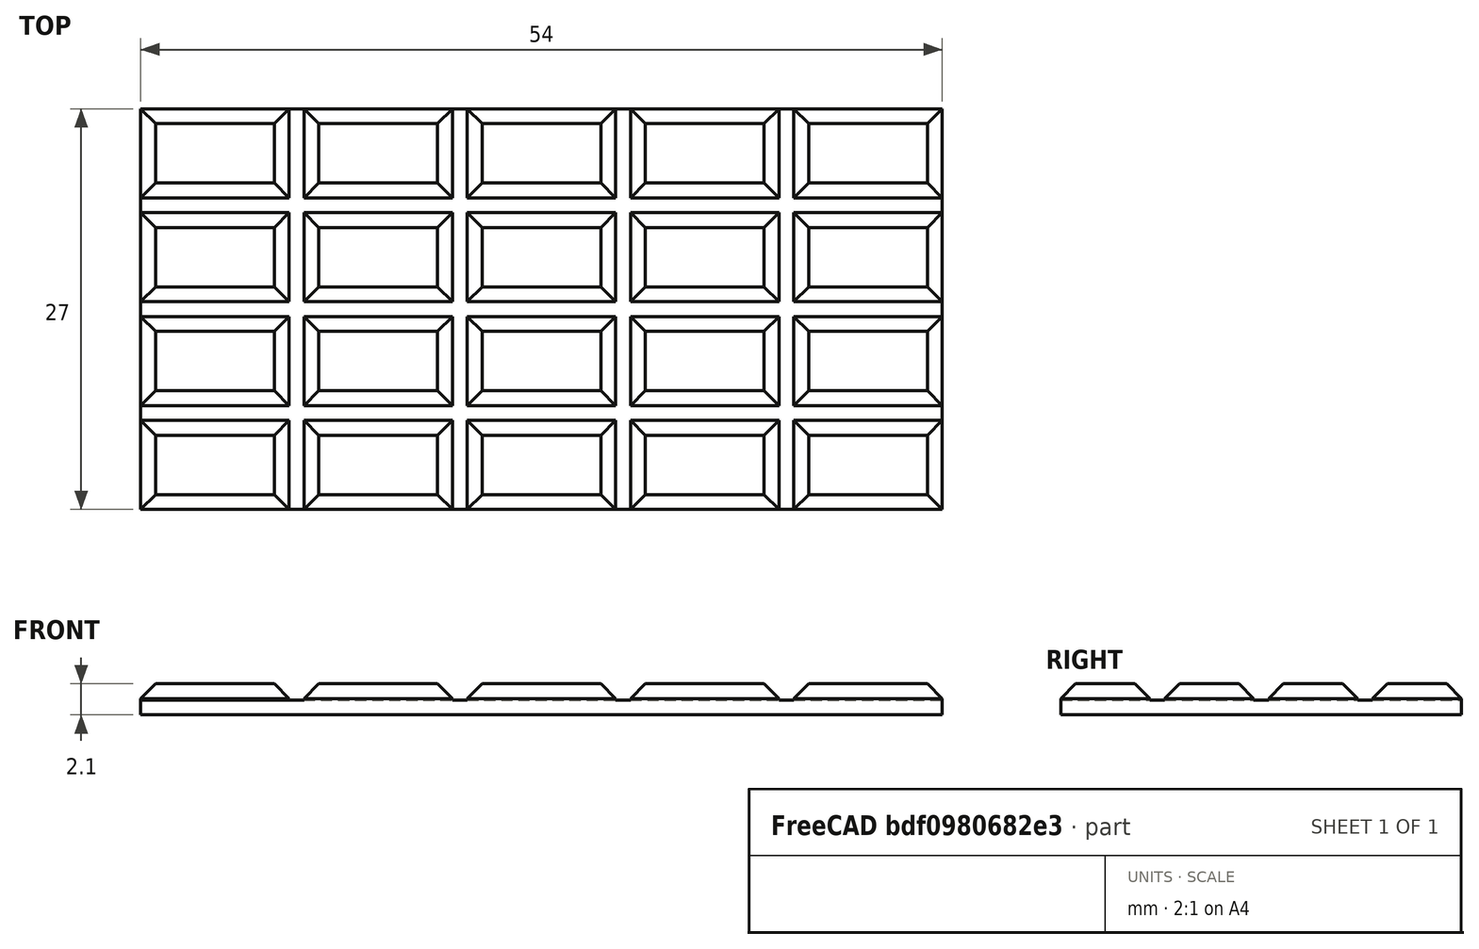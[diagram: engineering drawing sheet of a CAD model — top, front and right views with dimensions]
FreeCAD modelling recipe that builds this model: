
FCSTD DOCUMENT  (FreeCAD 0.21R33694 (Git))
Label: OJT1_T012_R01_xocolate
License: All rights reserved
LicenseURL: https://en.wikipedia.org/wiki/All_rights_reserved
objects: Part::Box×2, Part::Chamfer×1, Part::FeaturePython×1, Part::MultiFuse×1
note: 4 computed .brp shape members not serialized (recipe doc carries the construction recipe); baked Part::Feature solids carry a one-line shape summary decoded from their .brp

FEATURE [Part::Box] Box  label="Cub"
  AttacherType = Attacher::AttachEngine3D
  Height = 1
  Length = 54
  Width = 27
FEATURE [Part::Box] Box001  label="Cub001"
  AttacherType = Attacher::AttachEngine3D
  Height = 1.1
  Length = 10
  Placement = pos=(0,0,1) rot=(0,0,1;0rad)
  Width = 6
  expr: .Placement.Base.z = 1
FEATURE [Part::Chamfer] Chamfer
  Base = -> Box001
  Edges = 4 edges r=1: [Edge2,Edge6,Edge10,Edge12]
FEATURE [Part::FeaturePython] Array  # Draft array (typed FeaturePython)
  AlwaysSyncPlacement = false
  Angle = 360
  ArrayType = 0
  Axis = (0,0,1)
  Base = -> Chamfer
  Center = (0,0,0)
  Count = 20
  ExpandArray = false
  Fuse = false
  IntervalAxis = (0,0,0)
  IntervalX = (11,0,0)
  IntervalY = (0,7,0)
  IntervalZ = (0,0,100)
  NumberCircles = 3
  NumberPolar = 5
  NumberX = 5
  NumberY = 4
  NumberZ = 1
  PlacementList = 20 placements: [(0,0,0),(0,7,0),(0,14,0),(0,21,0),(11,0,0),(11,7,0),(11,14,0),(11,21,0),(22,0,0),(22,7,0),(22,14,0),(22,21,0),(33,0,0),(33,7,0),(33,14,0),(33,21,0),(44,0,0),(44,7,0),(44,14,0),(44,21,0)]
  RadialDistance = 50
  ScaleList = (20) [(1,1,1),(1,1,1),(1,1,1),(1,1,1),(1,1,1),(1,1,1),(1,1,1),(1,1,1),(1,1,1),(1,1,1),(1,1,1),(1,1,1),(1,1,1),(1,1,1),(1,1,1),(1,1,1),(1,1,1),(1,1,1),(1,1,1),(1,1,1)]
  Symmetry = 1
  TangentialDistance = 25
FEATURE [Part::MultiFuse] Fusion
  Shapes = -> [Box,Array]
